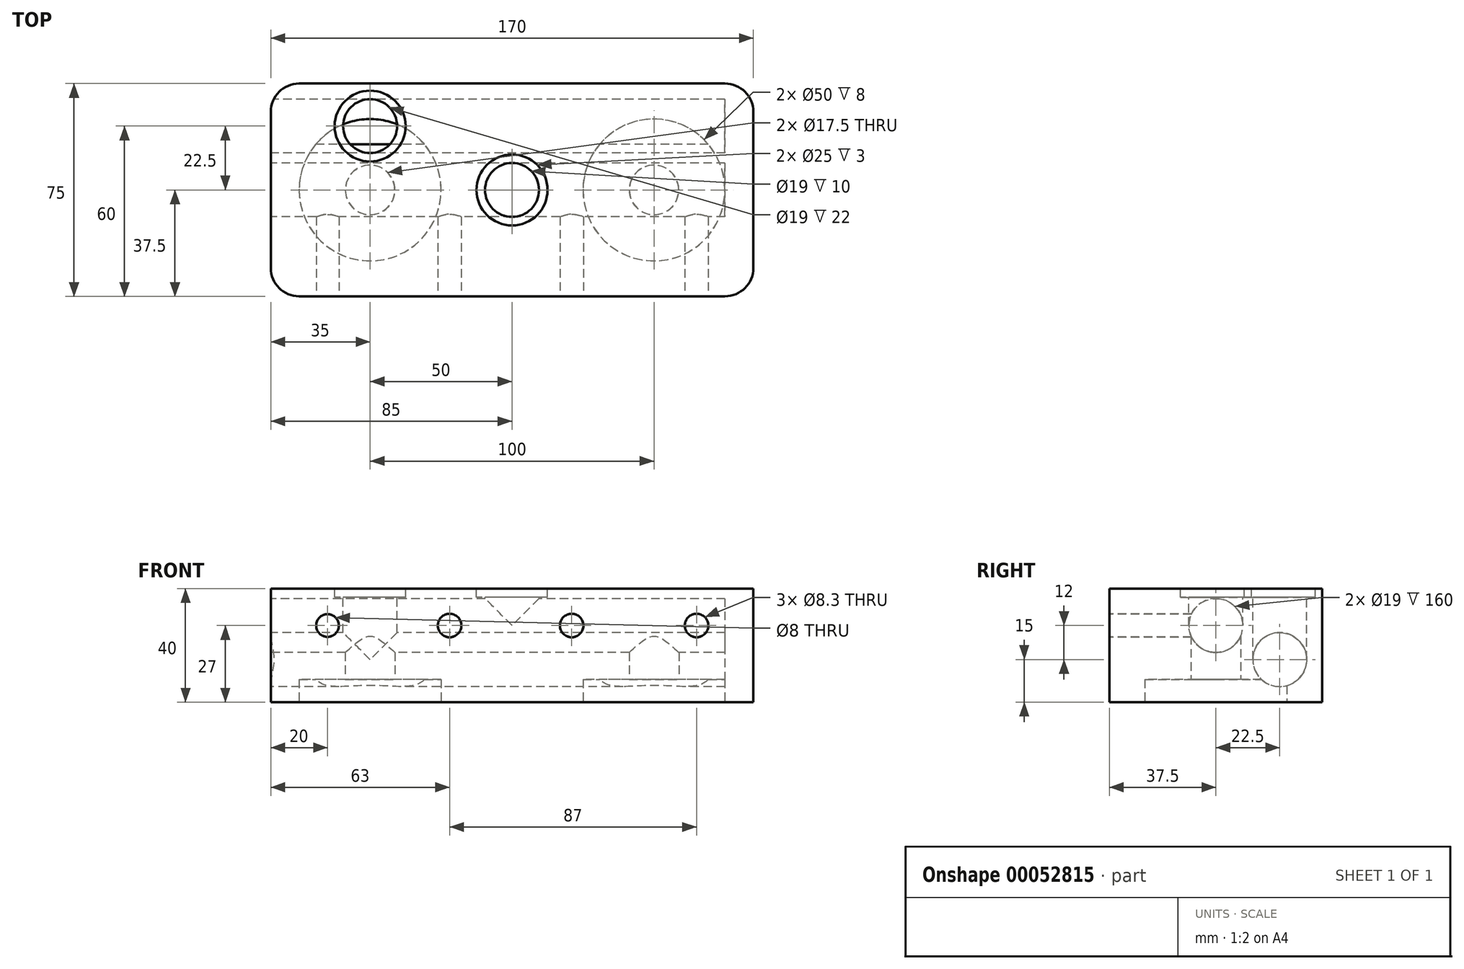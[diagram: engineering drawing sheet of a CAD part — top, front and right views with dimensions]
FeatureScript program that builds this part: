
annotation { "Feature Type Name" : "Feature", "Feature Type Description" : "" }
export const myFeature = defineFeature(function(context is Context, id is Id, definition is map)
    precondition{}
    {
        {
            var Q0;
            Q0=qCreatedBy(makeId("Top.planeOp"),FACE);
            var sketch = newSketch(context, id + "F0", { "sketchPlane" : qUnion([Q0])});
            skLineSegment(sketch, "E0.bottom", {"start": v(0, 0) * mm, "end": v(-170, 0) * mm});
            skLineSegment(sketch, "E0.top", {"start": v(0, 75) * mm, "end": v(-170, 75) * mm});
            skLineSegment(sketch, "E0.left", {"start": v(0, 0) * mm, "end": v(0, 75) * mm});
            skLineSegment(sketch, "E0.right", {"start": v(-170, 0) * mm, "end": v(-170, 75) * mm});
            skSolve(sketch);
        }
        {
            var Q0;
            Q0=makeQuery(id+"F0.imprint","IMPRINT",FACE,{"disambiguationData":[TD([[makeQuery(id+"F0.imprint","IMPRINT",EDGE,{"derivedFrom":sQuery(id+"F0.wireOp",EDGE,"E0.bottom")}),-1.0]])]});
            extrude(context, id + "F1", {"entities" : qUnion([Q0]), "depth" : 40 * mm});
        }
        {
            var Q0;
            Q0=makeQuery(id+"F1.opExtrude","SWEPT_EDGE",EDGE,{"disambiguationData":[OSD([sQuery(id+"F0.wireOp",EDGE,"E0.bottom"),sQuery(id+"F0.wireOp",EDGE,"E0.left")])]});
            var Q1;
            Q1=makeQuery(id+"F1.opExtrude","SWEPT_EDGE",EDGE,{"disambiguationData":[OSD([sQuery(id+"F0.wireOp",EDGE,"E0.top"),sQuery(id+"F0.wireOp",EDGE,"E0.left")])]});
            var Q2;
            Q2=makeQuery(id+"F1.opExtrude","SWEPT_EDGE",EDGE,{"disambiguationData":[OSD([sQuery(id+"F0.wireOp",EDGE,"E0.bottom"),sQuery(id+"F0.wireOp",EDGE,"E0.right")])]});
            var Q3;
            Q3=makeQuery(id+"F1.opExtrude","SWEPT_EDGE",EDGE,{"disambiguationData":[OSD([sQuery(id+"F0.wireOp",EDGE,"E0.top"),sQuery(id+"F0.wireOp",EDGE,"E0.right")])]});
            fillet(context, id + "F2", {"entities" : qUnion([Q0, Q1, Q2, Q3]), "radius" : 10 * mm, "tangentPropagation" : true, "allowEdgeOverflow" : false});
        }
        {
            var Q0;
            Q0=makeQuery(id+"F1.opExtrude","CAP_FACE",FACE,{"disambiguationData":[OSD([sQuery(id+"F0.wireOp",EDGE,"E0.bottom"),sQuery(id+"F0.wireOp",EDGE,"E0.top"),sQuery(id+"F0.wireOp",EDGE,"E0.left"),sQuery(id+"F0.wireOp",EDGE,"E0.right")])],"isStart":true});
            var sketch = newSketch(context, id + "F3", { "sketchPlane" : qUnion([Q0])});
            skCircle(sketch, "E1", {"center": v(-135, -37.5) * mm, "radius": 25 * mm});
            skCircle(sketch, "E2", {"center": v(-35, -37.5) * mm, "radius": 25 * mm});
            skCircle(sketch, "E3", {"center": v(-135, -37.5) * mm, "radius": 8.75 * mm});
            skCircle(sketch, "E4", {"center": v(-35, -37.5) * mm, "radius": 8.75 * mm});
            skSolve(sketch);
        }
        {
            var Q0;
            Q0=makeQuery(id+"F1.opExtrude","SWEPT_FACE",FACE,{"disambiguationData":[OSD([sQuery(id+"F0.wireOp",EDGE,"E0.right")])]});
            var sketch = newSketch(context, id + "F4", { "sketchPlane" : qUnion([Q0])});
            skCircle(sketch, "E5", {"center": v(-37.5, 27) * mm, "radius": 9.5 * mm});
            skCircle(sketch, "E6", {"center": v(-60, 15) * mm, "radius": 9.5 * mm});
            skSolve(sketch);
        }
        {
            var Q0;
            Q0=makeQuery(id+"F1.opExtrude","CAP_FACE",FACE,{"disambiguationData":[OSD([sQuery(id+"F0.wireOp",EDGE,"E0.bottom"),sQuery(id+"F0.wireOp",EDGE,"E0.top"),sQuery(id+"F0.wireOp",EDGE,"E0.left"),sQuery(id+"F0.wireOp",EDGE,"E0.right")])],"isStart":false});
            var sketch = newSketch(context, id + "F5", { "sketchPlane" : qUnion([Q0])});
            skCircle(sketch, "E7", {"center": v(-85, 37.5) * mm, "radius": 12.5 * mm});
            skCircle(sketch, "E8", {"center": v(-135, 60) * mm, "radius": 12.5 * mm});
            skCircle(sketch, "E9", {"center": v(-135, 60) * mm, "radius": 9.5 * mm});
            skCircle(sketch, "E10", {"center": v(-85, 37.5) * mm, "radius": 9.5 * mm});
            skSolve(sketch);
        }
        {
            var Q0;
            Q0=makeQuery(id+"F3.imprint","IMPRINT",FACE,{"disambiguationData":[TD([[makeQuery(id+"F3.imprint","IMPRINT",EDGE,{"derivedFrom":sQuery(id+"F3.wireOp",EDGE,"E1")}),1.0]])]});
            var Q1;
            Q1=makeQuery(id+"F3.imprint","IMPRINT",FACE,{"disambiguationData":[TD([[makeQuery(id+"F3.imprint","IMPRINT",EDGE,{"derivedFrom":sQuery(id+"F3.wireOp",EDGE,"E2")}),1.0]])]});
            extrude(context, id + "F6", {"entities" : qUnion([Q0, Q1]), "operationType" : NewBodyOperationType.REMOVE, "oppositeDirection" : true, "depth" : 8 * mm});
        }
        {
            var Q0;
            Q0=makeQuery(id+"F6.boolean.opBoolean","SPLIT",FACE,{"disambiguationData":[TD([makeQuery(id+"F6.opExtrude","SWEPT_FACE",FACE,{"disambiguationData":[OSD([sQuery(id+"F3.wireOp",EDGE,"E3")])]})])],"derivedFrom":makeQuery(id+"F1.opExtrude","CAP_FACE",FACE,{"disambiguationData":[OSD([sQuery(id+"F0.wireOp",EDGE,"E0.bottom"),sQuery(id+"F0.wireOp",EDGE,"E0.top"),sQuery(id+"F0.wireOp",EDGE,"E0.left"),sQuery(id+"F0.wireOp",EDGE,"E0.right")])],"isStart":true})});
            var Q1;
            Q1=makeQuery(id+"F6.boolean.opBoolean","SPLIT",FACE,{"disambiguationData":[TD([makeQuery(id+"F6.opExtrude","SWEPT_FACE",FACE,{"disambiguationData":[OSD([sQuery(id+"F3.wireOp",EDGE,"E4")])]})])],"derivedFrom":makeQuery(id+"F1.opExtrude","CAP_FACE",FACE,{"disambiguationData":[OSD([sQuery(id+"F0.wireOp",EDGE,"E0.bottom"),sQuery(id+"F0.wireOp",EDGE,"E0.top"),sQuery(id+"F0.wireOp",EDGE,"E0.left"),sQuery(id+"F0.wireOp",EDGE,"E0.right")])],"isStart":true})});
            extrude(context, id + "F7", {"entities" : qUnion([Q0, Q1]), "operationType" : NewBodyOperationType.REMOVE, "oppositeDirection" : true, "depth" : 27 * mm});
        }
        {
            var Q0;
            Q0=makeQuery(id+"F4.imprint","IMPRINT",FACE,{"disambiguationData":[TD([[makeQuery(id+"F4.imprint","IMPRINT",EDGE,{"derivedFrom":sQuery(id+"F4.wireOp",EDGE,"E5")}),1.0]])]});
            var Q1;
            {var subQ0=sQuery(id+"F4.wireOp",EDGE,"E6");var subQ1=sQuery(id+"F0.wireOp",EDGE,"E0.right");var subQ2=makeQuery(id+"F2.opFillet","BLEND_EDGE",EDGE,{"blendedFrom":[makeQuery(id+"F1.opExtrude","SWEPT_EDGE",EDGE,{"disambiguationData":[OSD([sQuery(id+"F0.wireOp",EDGE,"E0.top"),subQ1])]}),makeQuery(id+"F1.opExtrude","SWEPT_FACE",FACE,{"disambiguationData":[OSD([subQ1])]})],"blendedInto":[makeQuery(id+"F1.opExtrude","SWEPT_FACE",FACE,{"disambiguationData":[OSD([subQ1])]})]});var subQ3=makeQuery(id+"F4.imprint","INTERSECT",VERTEX,{"disambiguationData":[OD(0.0)],"derivedFrom":[subQ2,subQ0]});Q1=makeQuery(id+"F4.imprint","IMPRINT",FACE,{"disambiguationData":[TD([[makeQuery(id+"F4.imprint","IMPRINT",EDGE,{"disambiguationData":[TD([[subQ3,1.0]])],"derivedFrom":subQ0}),1.0]])]});}
            var Q2;
            {var subQ0=sQuery(id+"F4.wireOp",EDGE,"E6");var subQ1=sQuery(id+"F0.wireOp",EDGE,"E0.right");var subQ2=makeQuery(id+"F2.opFillet","BLEND_EDGE",EDGE,{"blendedFrom":[makeQuery(id+"F1.opExtrude","SWEPT_EDGE",EDGE,{"disambiguationData":[OSD([sQuery(id+"F0.wireOp",EDGE,"E0.top"),subQ1])]}),makeQuery(id+"F1.opExtrude","SWEPT_FACE",FACE,{"disambiguationData":[OSD([subQ1])]})],"blendedInto":[makeQuery(id+"F1.opExtrude","SWEPT_FACE",FACE,{"disambiguationData":[OSD([subQ1])]})]});var subQ3=makeQuery(id+"F4.imprint","INTERSECT",VERTEX,{"disambiguationData":[OD(0.0)],"derivedFrom":[subQ2,subQ0]});Q2=makeQuery(id+"F4.imprint","IMPRINT",FACE,{"disambiguationData":[TD([[makeQuery(id+"F4.imprint","IMPRINT",EDGE,{"disambiguationData":[TD([[subQ3,-1.0]])],"derivedFrom":subQ0}),1.0]])]});}
            extrude(context, id + "F8", {"entities" : qUnion([Q0, Q1, Q2]), "operationType" : NewBodyOperationType.REMOVE, "oppositeDirection" : true, "depth" : 160 * mm});
        }
        {
            var Q0;
            Q0=makeQuery(id+"F5.imprint","IMPRINT",FACE,{"disambiguationData":[TD([[makeQuery(id+"F5.imprint","IMPRINT",EDGE,{"derivedFrom":sQuery(id+"F5.wireOp",EDGE,"E8")}),1.0]])]});
            var Q1;
            Q1=makeQuery(id+"F5.imprint","IMPRINT",FACE,{"disambiguationData":[TD([[makeQuery(id+"F5.imprint","IMPRINT",EDGE,{"derivedFrom":sQuery(id+"F5.wireOp",EDGE,"E7")}),1.0]])]});
            extrude(context, id + "F9", {"entities" : qUnion([Q0, Q1]), "operationType" : NewBodyOperationType.REMOVE, "oppositeDirection" : true, "depth" : 3 * mm});
        }
        {
            var Q0;
            Q0=makeQuery(id+"F9.boolean.opBoolean","SPLIT",FACE,{"disambiguationData":[TD([makeQuery(id+"F9.opExtrude","SWEPT_FACE",FACE,{"disambiguationData":[OSD([sQuery(id+"F5.wireOp",EDGE,"E10")])]})])],"derivedFrom":makeQuery(id+"F1.opExtrude","CAP_FACE",FACE,{"disambiguationData":[OSD([sQuery(id+"F0.wireOp",EDGE,"E0.bottom"),sQuery(id+"F0.wireOp",EDGE,"E0.top"),sQuery(id+"F0.wireOp",EDGE,"E0.left"),sQuery(id+"F0.wireOp",EDGE,"E0.right")])],"isStart":false})});
            extrude(context, id + "F10", {"entities" : qUnion([Q0]), "operationType" : NewBodyOperationType.REMOVE, "oppositeDirection" : true, "depth" : 13 * mm});
        }
        {
            var Q0;
            Q0=makeQuery(id+"F9.boolean.opBoolean","SPLIT",FACE,{"disambiguationData":[TD([makeQuery(id+"F9.opExtrude","SWEPT_FACE",FACE,{"disambiguationData":[OSD([sQuery(id+"F5.wireOp",EDGE,"E9")])]})])],"derivedFrom":makeQuery(id+"F1.opExtrude","CAP_FACE",FACE,{"disambiguationData":[OSD([sQuery(id+"F0.wireOp",EDGE,"E0.bottom"),sQuery(id+"F0.wireOp",EDGE,"E0.top"),sQuery(id+"F0.wireOp",EDGE,"E0.left"),sQuery(id+"F0.wireOp",EDGE,"E0.right")])],"isStart":false})});
            extrude(context, id + "F11", {"entities" : qUnion([Q0]), "operationType" : NewBodyOperationType.REMOVE, "oppositeDirection" : true, "depth" : 25 * mm});
        }
        {
            var Q0;
            Q0=makeQuery(id+"F1.opExtrude","SWEPT_FACE",FACE,{"disambiguationData":[OSD([sQuery(id+"F0.wireOp",EDGE,"E0.bottom")])]});
            var sketch = newSketch(context, id + "F12", { "sketchPlane" : qUnion([Q0])});
            skCircle(sketch, "E11", {"center": v(-150, 27) * mm, "radius": 4 * mm});
            skCircle(sketch, "E12", {"center": v(-107, 27) * mm, "radius": 4.15 * mm});
            skCircle(sketch, "E13", {"center": v(-64, 27) * mm, "radius": 4.15 * mm});
            skCircle(sketch, "E14", {"center": v(-20, 27) * mm, "radius": 4.15 * mm});
            skSolve(sketch);
        }
        {
            var Q0;
            Q0=makeQuery(id+"F12.imprint","IMPRINT",FACE,{"disambiguationData":[TD([[makeQuery(id+"F12.imprint","IMPRINT",EDGE,{"derivedFrom":sQuery(id+"F12.wireOp",EDGE,"E11")}),1.0]])]});
            var Q1;
            Q1=makeQuery(id+"F12.imprint","IMPRINT",FACE,{"disambiguationData":[TD([[makeQuery(id+"F12.imprint","IMPRINT",EDGE,{"derivedFrom":sQuery(id+"F12.wireOp",EDGE,"E12")}),1.0]])]});
            var Q2;
            Q2=makeQuery(id+"F12.imprint","IMPRINT",FACE,{"disambiguationData":[TD([[makeQuery(id+"F12.imprint","IMPRINT",EDGE,{"derivedFrom":sQuery(id+"F12.wireOp",EDGE,"E13")}),1.0]])]});
            var Q3;
            Q3=makeQuery(id+"F12.imprint","IMPRINT",FACE,{"disambiguationData":[TD([[makeQuery(id+"F12.imprint","IMPRINT",EDGE,{"derivedFrom":sQuery(id+"F12.wireOp",EDGE,"E14")}),1.0]])]});
            extrude(context, id + "F13", {"entities" : qUnion([Q0, Q1, Q2, Q3]), "operationType" : NewBodyOperationType.REMOVE, "oppositeDirection" : true, "depth" : 35 * mm});
        }
    });
